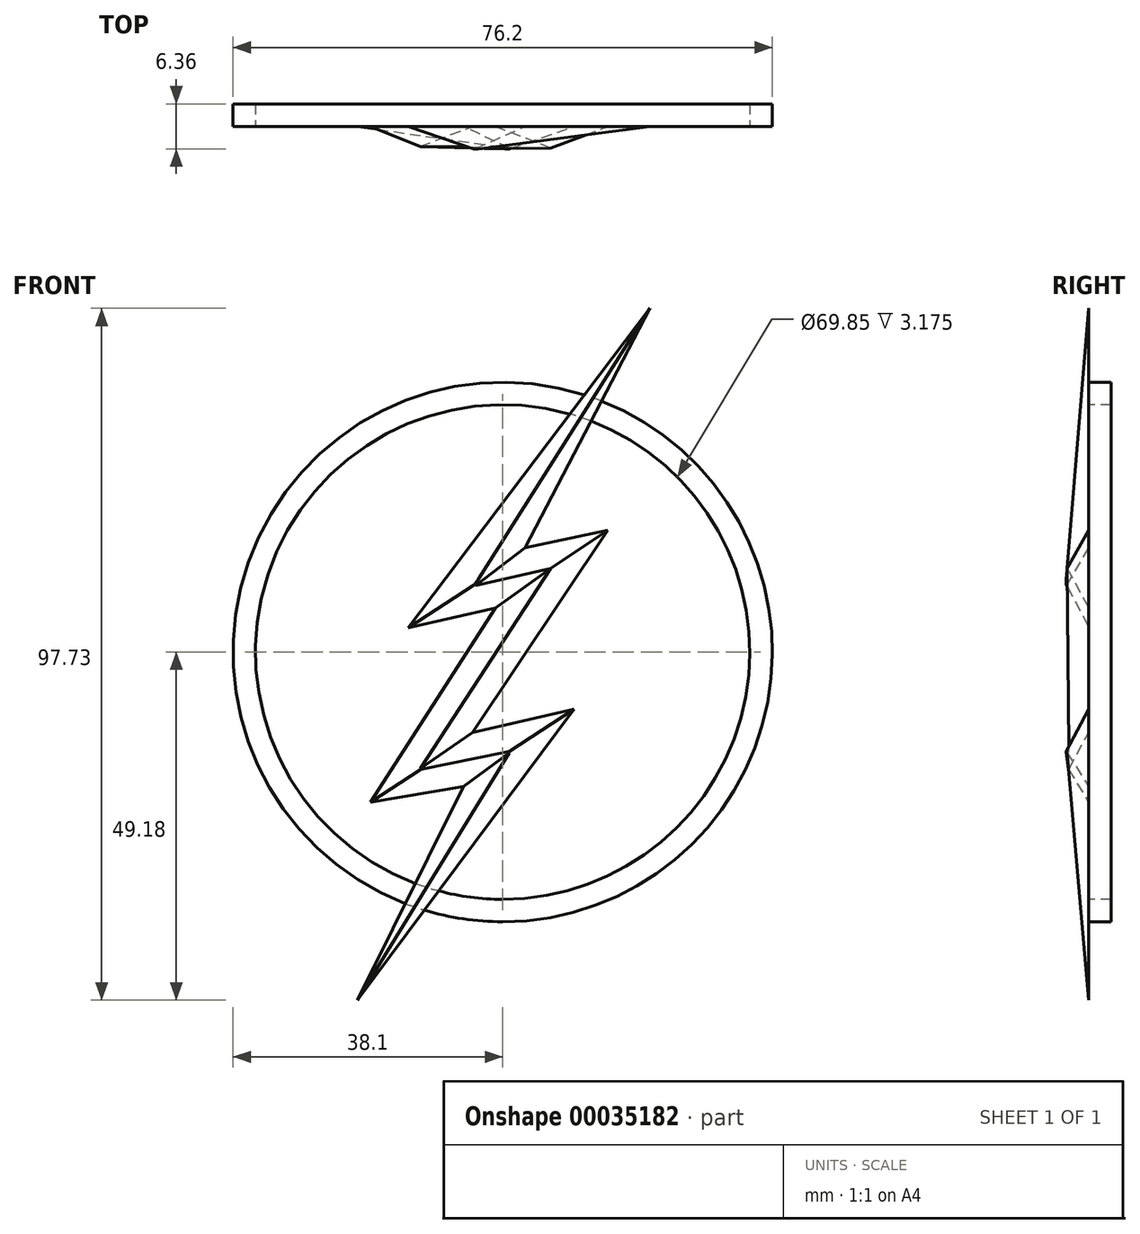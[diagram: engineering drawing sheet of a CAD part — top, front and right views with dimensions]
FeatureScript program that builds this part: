
annotation { "Feature Type Name" : "Feature", "Feature Type Description" : "" }
export const myFeature = defineFeature(function(context is Context, id is Id, definition is map)
    precondition{}
    {
        {
            var Q0;
            Q0=qCreatedBy(makeId("Front.planeOp"),FACE);
            var sketch = newSketch(context, id + "F0", { "sketchPlane" : qUnion([Q0])});
            skCircle(sketch, "E0", {"center": v(0, 0) * mm, "radius": 38.1 * mm});
            skCircle(sketch, "E1.0", {"center": v(0, 0) * mm, "radius": 34.93 * mm});
            skSolve(sketch);
        }
        {
            var Q0;
            Q0=makeQuery(id+"F0.imprint","IMPRINT",FACE,{"disambiguationData":[TD([[makeQuery(id+"F0.imprint","IMPRINT",EDGE,{"derivedFrom":sQuery(id+"F0.wireOp",EDGE,"E0")}),1.0]])]});
            extrude(context, id + "F1", {"entities" : qUnion([Q0]), "oppositeDirection" : true, "depth" : 3.17 * mm});
        }
        {
            var Q0;
            Q0=qCreatedBy(makeId("Front.planeOp"),FACE);
            var sketch = newSketch(context, id + "F2", { "sketchPlane" : qUnion([Q0])});
            skLineSegment(sketch, "E2", {"start": v(20.81, 48.55) * mm, "end": v(-13.36, 3.44) * mm});
            skLineSegment(sketch, "E3", {"start": v(20.81, 48.55) * mm, "end": v(3.14, 14.7) * mm});
            skLineSegment(sketch, "E4", {"start": v(3.14, 14.7) * mm, "end": v(14.83, 17.23) * mm});
            skLineSegment(sketch, "E5", {"start": v(14.83, 17.23) * mm, "end": v(-4.25, -11.35) * mm});
            skLineSegment(sketch, "E6", {"start": v(-4.25, -11.35) * mm, "end": v(10.08, -8.07) * mm});
            skLineSegment(sketch, "E7", {"start": v(10.08, -8.07) * mm, "end": v(-20.51, -49.18) * mm});
            skLineSegment(sketch, "E8", {"start": v(-13.36, 3.44) * mm, "end": v(-1.06, 6.25) * mm});
            skLineSegment(sketch, "E9", {"start": v(-1.06, 6.25) * mm, "end": v(-18.67, -21.24) * mm});
            skLineSegment(sketch, "E10", {"start": v(-18.67, -21.24) * mm, "end": v(-5.51, -19.01) * mm});
            skLineSegment(sketch, "E11", {"start": v(-5.51, -19.01) * mm, "end": v(-20.51, -49.18) * mm});
            skPoint(sketch, "E12", {"position": v(-10.95, -15.7) * mm});
            skPoint(sketch, "E13", {"position": v(2.06, -13.67) * mm});
            skPoint(sketch, "E14", {"position": v(5.45, 10.7) * mm});
            skPoint(sketch, "E15", {"position": v(-5.04, 8.9) * mm});
            skLineSegment(sketch, "E16", {"start": v(-5.04, 8.9) * mm, "end": v(5.45, 10.7) * mm});
            skLineSegment(sketch, "E17", {"start": v(-10.95, -15.7) * mm, "end": v(2.06, -13.67) * mm});
            skLineSegment(sketch, "E18", {"start": v(-5.04, 8.9) * mm, "end": v(20.81, 48.55) * mm});
            skLineSegment(sketch, "E19", {"start": v(5.45, 10.7) * mm, "end": v(-10.95, -15.7) * mm});
            skLineSegment(sketch, "E20", {"start": v(2.06, -13.67) * mm, "end": v(-20.51, -49.18) * mm});
            skLineSegment(sketch, "E21", {"start": v(-5.04, 8.9) * mm, "end": v(-13.36, 3.44) * mm});
            skLineSegment(sketch, "E22", {"start": v(3.14, 14.7) * mm, "end": v(-5.04, 8.9) * mm});
            skLineSegment(sketch, "E23", {"start": v(5.45, 10.7) * mm, "end": v(14.83, 17.23) * mm});
            skLineSegment(sketch, "E24", {"start": v(-1.06, 6.25) * mm, "end": v(5.45, 10.7) * mm});
            skLineSegment(sketch, "E25", {"start": v(-10.95, -15.7) * mm, "end": v(-4.25, -11.35) * mm});
            skLineSegment(sketch, "E26", {"start": v(2.06, -13.67) * mm, "end": v(10.08, -8.07) * mm});
            skLineSegment(sketch, "E27", {"start": v(-5.51, -19.01) * mm, "end": v(2.06, -13.67) * mm});
            skLineSegment(sketch, "E28", {"start": v(-10.95, -15.7) * mm, "end": v(-18.67, -21.24) * mm});
            skSolve(sketch);
        }
        {
            var Q0;
            Q0 = qSketchRegion(id + "F2", true);
            extrude(context, id + "F3", {"entities" : qUnion([Q0]), "depth" : 3.17 * mm, "hasDraft" : true, "draftAngle" : 50 * degree, "draftPullDirection" : true});
        }
    });
